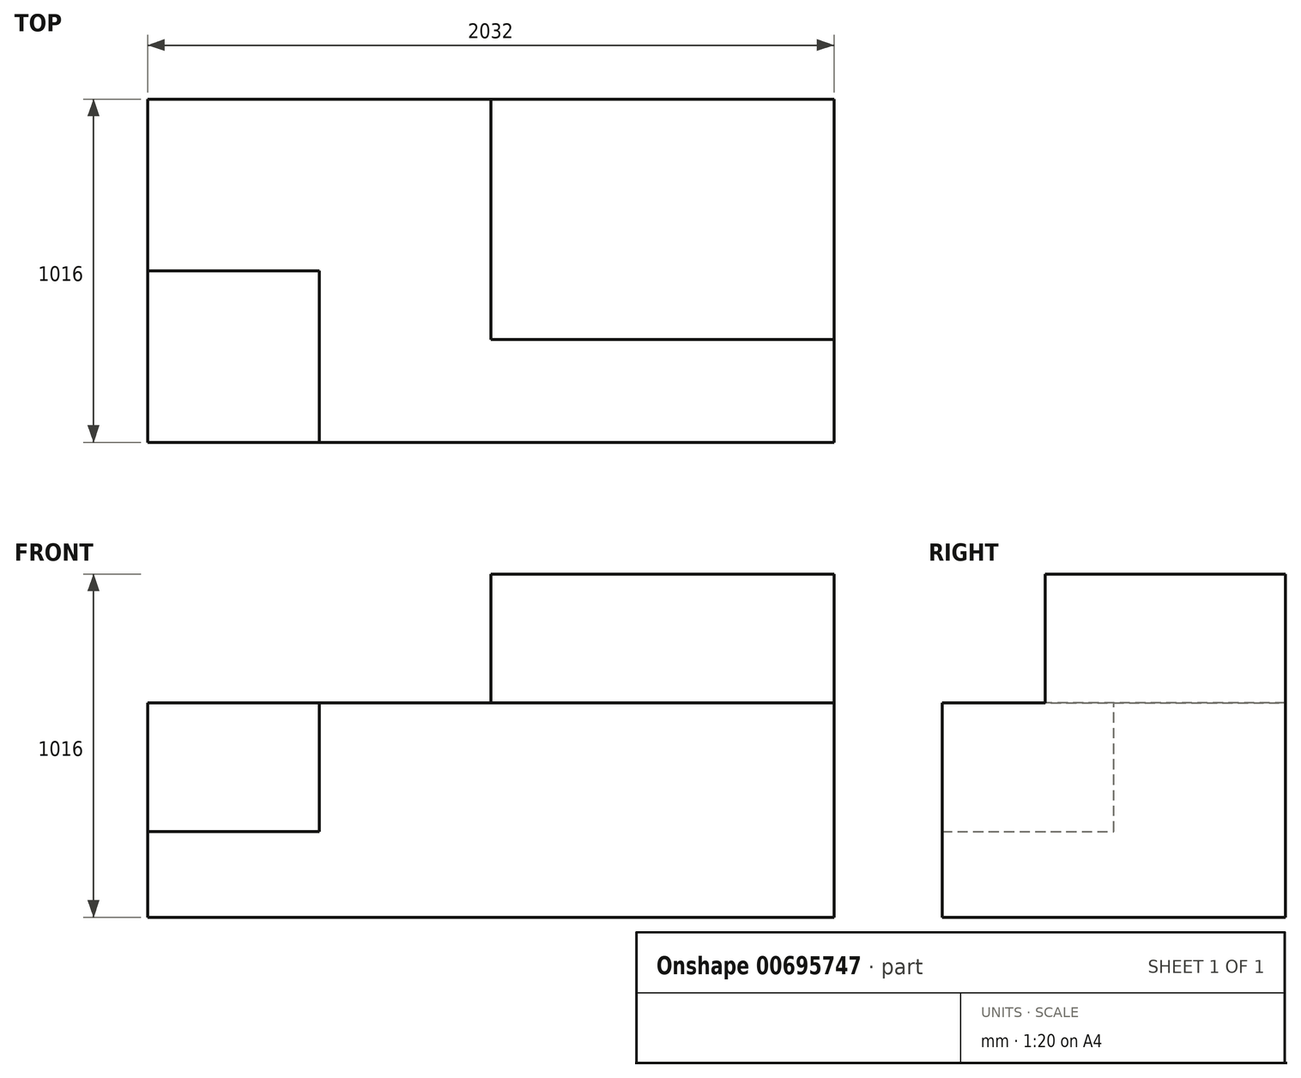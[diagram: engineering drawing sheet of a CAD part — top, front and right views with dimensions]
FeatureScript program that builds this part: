
annotation { "Feature Type Name" : "Feature", "Feature Type Description" : "" }
export const myFeature = defineFeature(function(context is Context, id is Id, definition is map)
    precondition{}
    {
        {
            var Q0;
            Q0=qCreatedBy(makeId("Front.planeOp"),FACE);
            var sketch = newSketch(context, id + "F0", { "sketchPlane" : qUnion([Q0])});
            skLineSegment(sketch, "E0.bottom", {"start": v(-916.75, 469.46) * mm, "end": v(1115.25, 469.46) * mm});
            skLineSegment(sketch, "E0.top", {"start": v(-916.75, -419.54) * mm, "end": v(1115.25, -419.54) * mm});
            skLineSegment(sketch, "E0.left", {"start": v(-916.75, 469.46) * mm, "end": v(-916.75, -419.54) * mm});
            skLineSegment(sketch, "E0.right", {"start": v(1115.25, 469.46) * mm, "end": v(1115.25, -419.54) * mm});
            skSolve(sketch);
        }
        {
            var Q0;
            Q0=makeQuery(id+"F0.imprint","IMPRINT",FACE,{"disambiguationData":[TD([[makeQuery(id+"F0.imprint","IMPRINT",EDGE,{"derivedFrom":sQuery(id+"F0.wireOp",EDGE,"E0.bottom")}),-1.0]])]});
            extrude(context, id + "F1", {"entities" : qUnion([Q0]), "depth" : 1016 * mm, "offsetDistance" : 25.4 * mm});
        }
        {
            var Q0;
            Q0=makeQuery(id+"F1.opExtrude","SWEPT_FACE",FACE,{"disambiguationData":[OSD([sQuery(id+"F0.wireOp",EDGE,"E0.bottom")])]});
            var sketch = newSketch(context, id + "F2", { "sketchPlane" : qUnion([Q0])});
            skLineSegment(sketch, "E1.bottom", {"start": v(1115.25, 0) * mm, "end": v(99.25, 0) * mm});
            skLineSegment(sketch, "E1.top", {"start": v(1115.25, -711.2) * mm, "end": v(99.25, -711.2) * mm});
            skLineSegment(sketch, "E1.left", {"start": v(1115.25, 0) * mm, "end": v(1115.25, -711.2) * mm});
            skLineSegment(sketch, "E1.right", {"start": v(99.25, 0) * mm, "end": v(99.25, -711.2) * mm});
            skSolve(sketch);
        }
        {
            var Q0;
            Q0 = qSketchRegion(id + "F2", true);
            var Q1;
            Q1=makeQuery(id+"F2.imprint","IMPRINT",FACE,{"disambiguationData":[TD([[makeQuery(id+"F2.imprint","IMPRINT",EDGE,{"derivedFrom":sQuery(id+"F2.wireOp",EDGE,"E1.bottom")}),-1.0]])]});
            extrude(context, id + "F3", {"entities" : qUnion([Q0, Q1]), "operationType" : NewBodyOperationType.ADD, "depth" : 381 * mm, "offsetDistance" : 25.4 * mm});
        }
        {
            var Q0;
            Q0=makeQuery(id+"F1.opExtrude","SWEPT_FACE",FACE,{"disambiguationData":[OSD([sQuery(id+"F0.wireOp",EDGE,"E0.bottom")])]});
            var sketch = newSketch(context, id + "F4", { "sketchPlane" : qUnion([Q0])});
            skLineSegment(sketch, "E2.bottom", {"start": v(-916.75, -1016) * mm, "end": v(-408.75, -1016) * mm});
            skLineSegment(sketch, "E2.top", {"start": v(-916.75, -508) * mm, "end": v(-408.75, -508) * mm});
            skLineSegment(sketch, "E2.left", {"start": v(-916.75, -1016) * mm, "end": v(-916.75, -508) * mm});
            skLineSegment(sketch, "E2.right", {"start": v(-408.75, -1016) * mm, "end": v(-408.75, -508) * mm});
            skSolve(sketch);
        }
        {
            var Q0;
            Q0 = qSketchRegion(id + "F4", true);
            extrude(context, id + "F5", {"entities" : qUnion([Q0]), "operationType" : NewBodyOperationType.REMOVE, "oppositeDirection" : true, "depth" : 381 * mm, "offsetDistance" : 25.4 * mm});
        }
        {
            var Q0;
            Q0=makeQuery(id+"F1.opExtrude","SWEPT_FACE",FACE,{"disambiguationData":[OSD([sQuery(id+"F0.wireOp",EDGE,"E0.top")])]});
            var sketch = newSketch(context, id + "F6", { "sketchPlane" : qUnion([Q0])});
            skLineSegment(sketch, "E3.bottom", {"start": v(-916.75, 1016) * mm, "end": v(1115.25, 1016) * mm});
            skLineSegment(sketch, "E3.top", {"start": v(-916.75, 0) * mm, "end": v(1115.25, 0) * mm});
            skLineSegment(sketch, "E3.left", {"start": v(-916.75, 1016) * mm, "end": v(-916.75, 0) * mm});
            skLineSegment(sketch, "E3.right", {"start": v(1115.25, 1016) * mm, "end": v(1115.25, 0) * mm});
            skSolve(sketch);
        }
        {
            var Q0;
            Q0=makeQuery(id+"F6.imprint","IMPRINT",FACE,{"disambiguationData":[TD([[makeQuery(id+"F6.imprint","IMPRINT",EDGE,{"derivedFrom":sQuery(id+"F6.wireOp",EDGE,"E3.bottom")}),-1.0]])]});
            extrude(context, id + "F7", {"entities" : qUnion([Q0]), "operationType" : NewBodyOperationType.REMOVE, "oppositeDirection" : true, "depth" : 254 * mm, "offsetDistance" : 25.4 * mm});
        }
    });
